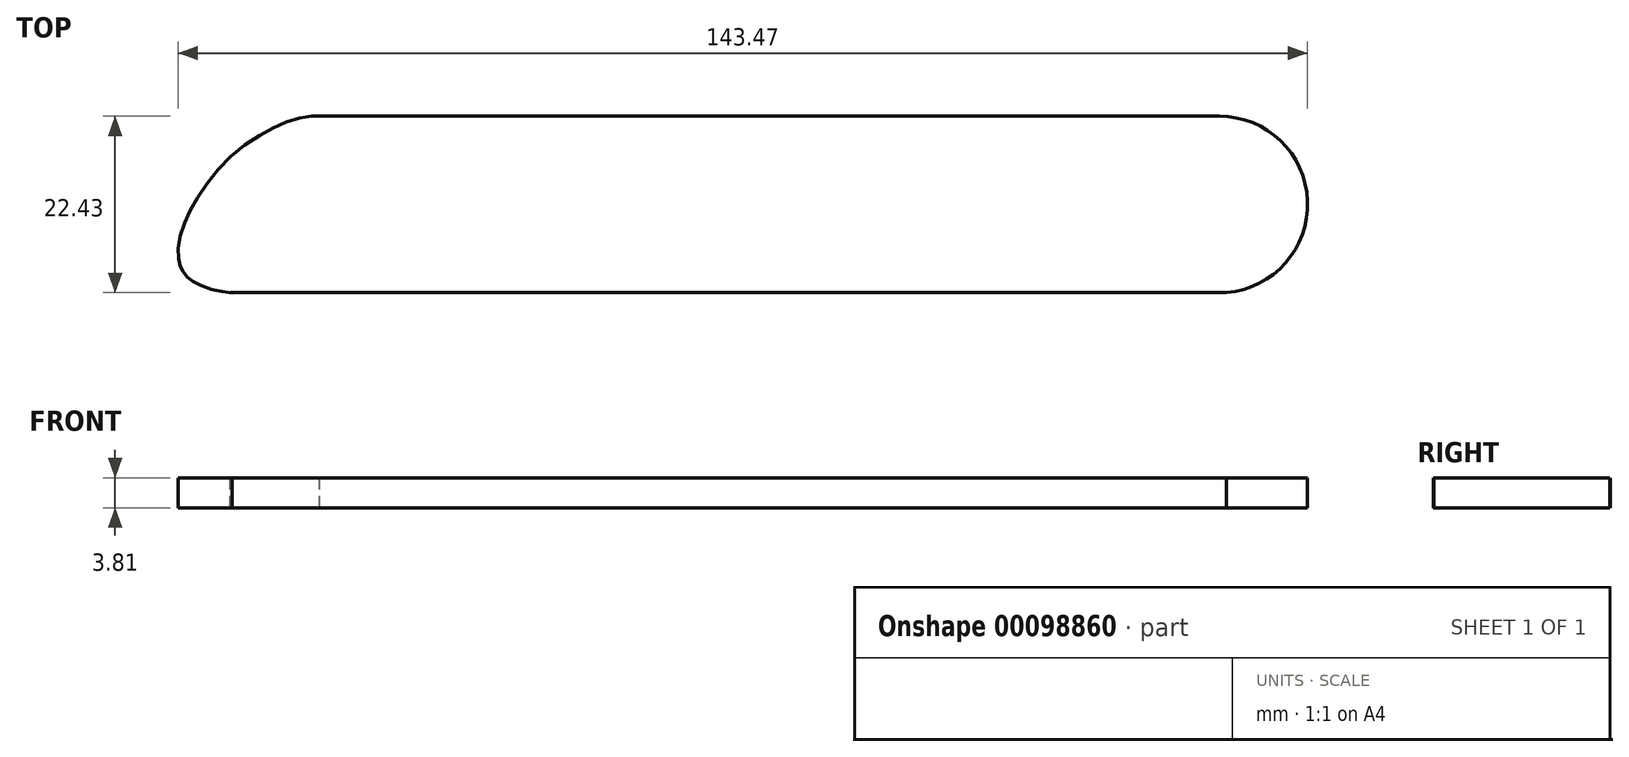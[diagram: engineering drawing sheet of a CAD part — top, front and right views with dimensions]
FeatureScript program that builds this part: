
annotation { "Feature Type Name" : "Feature", "Feature Type Description" : "" }
export const myFeature = defineFeature(function(context is Context, id is Id, definition is map)
    precondition{}
    {
        {
            var Q0;
            Q0=qCreatedBy(makeId("Top.planeOp"),FACE);
            var sketch = newSketch(context, id + "F0", { "sketchPlane" : qUnion([Q0])});
            skLineSegment(sketch, "E0", {"start": v(-54.63, 15.48) * mm, "end": v(59.67, 15.48) * mm});
            skLineSegment(sketch, "E1", {"start": v(-66.22, -16.12) * mm, "end": v(60.78, -16.12) * mm});
            skArc(sketch, "E2", {"start": v(60.78, -16.12) * mm, "mid": v(75.48, 0.21) * mm, "end": v(59.67, 15.48) * mm});
            skFitSpline(sketch, "E3", {"points": [v(-54.63, 15.48) * mm, v(-66.22, -16.12) * mm], "startDerivative": vector(-49.63, 0) * mm, "endDerivative": vector(69.03, -7.39) * mm});
            skLineSegment(sketch, "E4.0", {"start": v(-65.97, -11.53) * mm, "end": v(60.6, -11.53) * mm});
            skFitSpline(sketch, "E4.1", {"points": [v(-54.63, 10.88) * mm, v(-55.33, 10.88) * mm, v(-56.78, 10.73) * mm, v(-59.13, 10.02) * mm, v(-61.53, 8.86) * mm, v(-64.7, 6.75) * mm, v(-67.59, 3.98) * mm, v(-69.87, 0.9) * mm, v(-71.2, -1.43) * mm, v(-72.1, -3.67) * mm, v(-72.54, -5.67) * mm, v(-72.55, -7) * mm, v(-72.4, -7.85) * mm, v(-72.22, -8.39) * mm, v(-71.98, -8.85) * mm, v(-71.66, -9.28) * mm, v(-71.23, -9.7) * mm, v(-70.64, -10.15) * mm, v(-69.82, -10.58) * mm, v(-68.4, -11.12) * mm, v(-66.92, -11.43) * mm, v(-65.74, -11.55) * mm]});
            skLineSegment(sketch, "E4.2", {"start": v(-54.63, 10.88) * mm, "end": v(59.67, 10.88) * mm});
            skArc(sketch, "E4.3", {"start": v(60.6, -11.53) * mm, "mid": v(70.88, 0.12) * mm, "end": v(59.67, 10.88) * mm});
            skLineSegment(sketch, "E5.0", {"start": v(-59.75, -76.74) * mm, "end": v(66.82, -76.74) * mm});
            skFitSpline(sketch, "E5.1", {"points": [v(-48.41, -54.33) * mm, v(-49.1, -54.33) * mm, v(-50.56, -54.48) * mm, v(-52.9, -55.19) * mm, v(-55.31, -56.36) * mm, v(-58.48, -58.46) * mm, v(-61.37, -61.24) * mm, v(-63.65, -64.3) * mm, v(-64.98, -66.64) * mm, v(-65.88, -68.88) * mm, v(-66.32, -70.88) * mm, v(-66.33, -72.22) * mm, v(-66.17, -73.07) * mm, v(-66, -73.6) * mm, v(-65.76, -74.06) * mm, v(-65.44, -74.5) * mm, v(-65.01, -74.92) * mm, v(-64.42, -75.36) * mm, v(-63.6, -75.8) * mm, v(-62.18, -76.33) * mm, v(-60.7, -76.64) * mm, v(-59.51, -76.76) * mm]});
            skLineSegment(sketch, "E5.2", {"start": v(-48.41, -54.33) * mm, "end": v(65.9, -54.33) * mm});
            skArc(sketch, "E5.3", {"start": v(66.82, -76.74) * mm, "mid": v(77.1, -65.09) * mm, "end": v(65.9, -54.33) * mm});
            skSolve(sketch);
        }
        {
            var Q0;
            Q0=sQuery(id+"F0.wireOp",EDGE,"E5.0");
            var Q1;
            Q1=sQuery(id+"F0.wireOp",EDGE,"E5.3");
            var Q2;
            Q2=sQuery(id+"F0.wireOp",EDGE,"E5.2");
            var Q3;
            Q3=sQuery(id+"F0.wireOp",EDGE,"E5.1");
            extrude(context, id + "F1", {"bodyType" : ToolBodyType.SURFACE, "surfaceEntities" : qUnion([Q0, Q1, Q2, Q3]), "depth" : 3.8 * mm});
        }
    });
